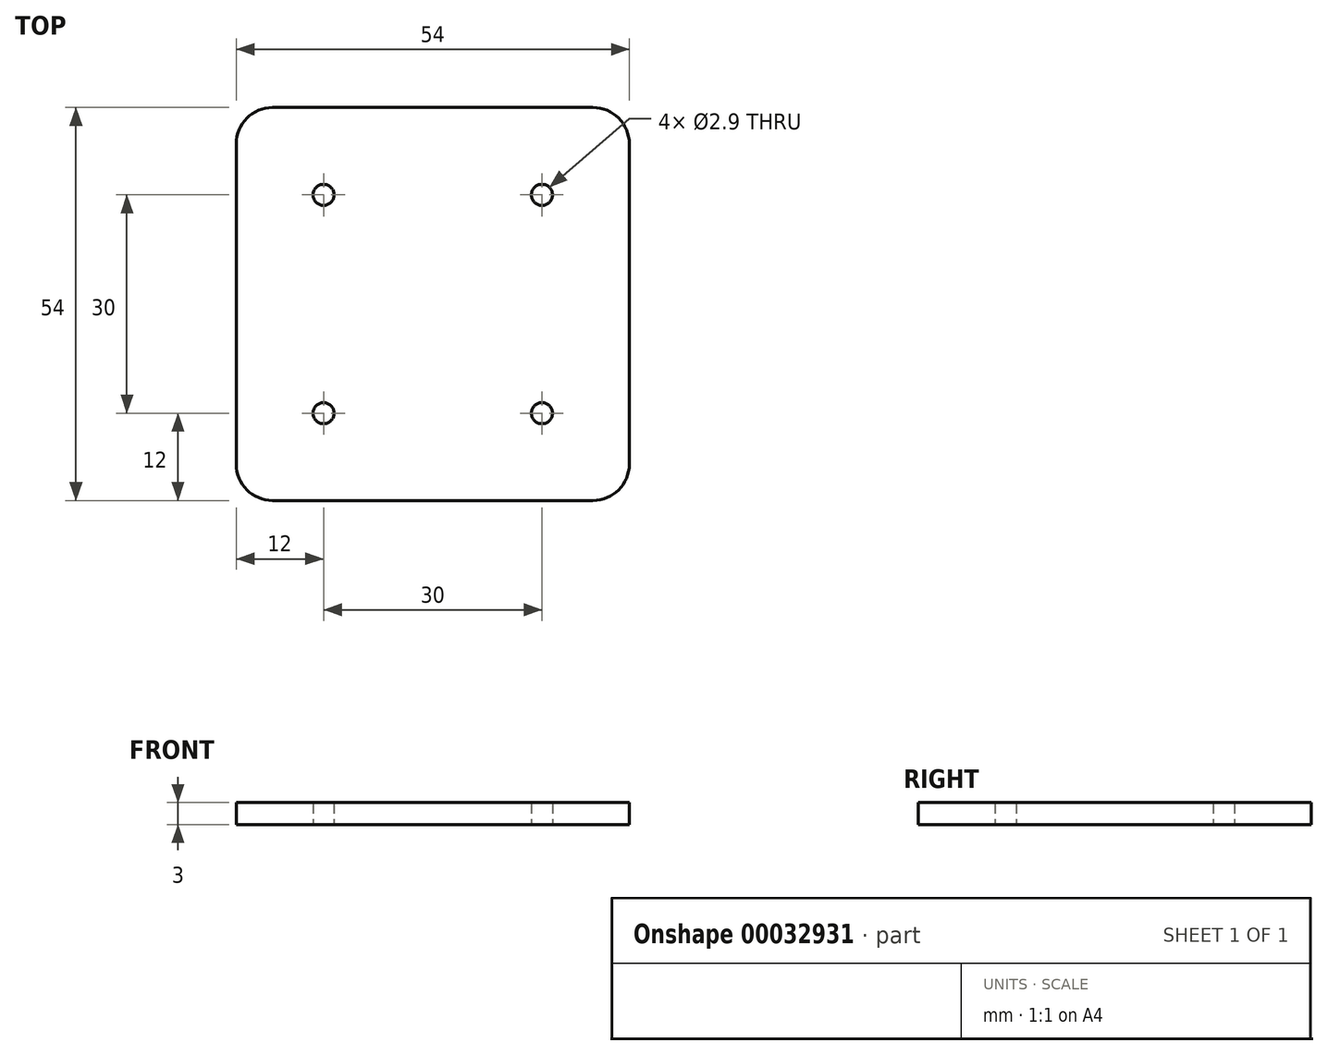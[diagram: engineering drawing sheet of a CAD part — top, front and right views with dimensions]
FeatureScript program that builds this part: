
annotation { "Feature Type Name" : "Feature", "Feature Type Description" : "" }
export const myFeature = defineFeature(function(context is Context, id is Id, definition is map)
    precondition{}
    {
        {
            var Q0;
            Q0=qCreatedBy(makeId("Top.planeOp"),FACE);
            var sketch = newSketch(context, id + "F0", { "sketchPlane" : qUnion([Q0])});
            skLineSegment(sketch, "E0.rect.bottom", {"start": v(22, -27) * mm, "end": v(-22, -27) * mm});
            skLineSegment(sketch, "E0.rect.top", {"start": v(22, 27) * mm, "end": v(-22, 27) * mm});
            skLineSegment(sketch, "E0.rect.left", {"start": v(27, -22) * mm, "end": v(27, 22) * mm});
            skLineSegment(sketch, "E0.rect.right", {"start": v(-27, -22) * mm, "end": v(-27, 22) * mm});
            skPoint(sketch, "E0.rect.middle", {"position": v(0, 0) * mm});
            skLineSegment(sketch, "E1.rect.bottom", {"start": v(15, -15) * mm, "end": v(-15, -15) * mm, "construction": true});
            skLineSegment(sketch, "E1.rect.top", {"start": v(15, 15) * mm, "end": v(-15, 15) * mm, "construction": true});
            skLineSegment(sketch, "E1.rect.left", {"start": v(15, -15) * mm, "end": v(15, 15) * mm, "construction": true});
            skLineSegment(sketch, "E1.rect.right", {"start": v(-15, -15) * mm, "end": v(-15, 15) * mm, "construction": true});
            skCircle(sketch, "E2", {"center": v(15, 15) * mm, "radius": 1.45 * mm});
            skCircle(sketch, "E3.MirrorC", {"center": v(-15, 15) * mm, "radius": 1.45 * mm});
            skCircle(sketch, "E4.MirrorC", {"center": v(-15, -15) * mm, "radius": 1.45 * mm});
            skCircle(sketch, "E5.MirrorC", {"center": v(15, -15) * mm, "radius": 1.45 * mm});
            skPoint(sketch, "E6.visualSharp", {"position": v(-27, 27) * mm});
            skArc(sketch, "E6.filletArc", {"start": v(-22, 27) * mm, "mid": v(-25.54, 25.54) * mm, "end": v(-27, 22) * mm});
            skPoint(sketch, "E7.visualSharp", {"position": v(27, 27) * mm});
            skArc(sketch, "E7.filletArc", {"start": v(27, 22) * mm, "mid": v(25.54, 25.54) * mm, "end": v(22, 27) * mm});
            skPoint(sketch, "E8.visualSharp", {"position": v(27, -27) * mm});
            skArc(sketch, "E8.filletArc", {"start": v(22, -27) * mm, "mid": v(25.54, -25.54) * mm, "end": v(27, -22) * mm});
            skPoint(sketch, "E9.visualSharp", {"position": v(-27, -27) * mm});
            skArc(sketch, "E9.filletArc", {"start": v(-27, -22) * mm, "mid": v(-25.54, -25.54) * mm, "end": v(-22, -27) * mm});
            skSolve(sketch);
        }
        {
            var Q0;
            Q0 = qSketchRegion(id + "F0", true);
            extrude(context, id + "F1", {"entities" : qUnion([Q0]), "depth" : 3 * mm});
        }
    });
